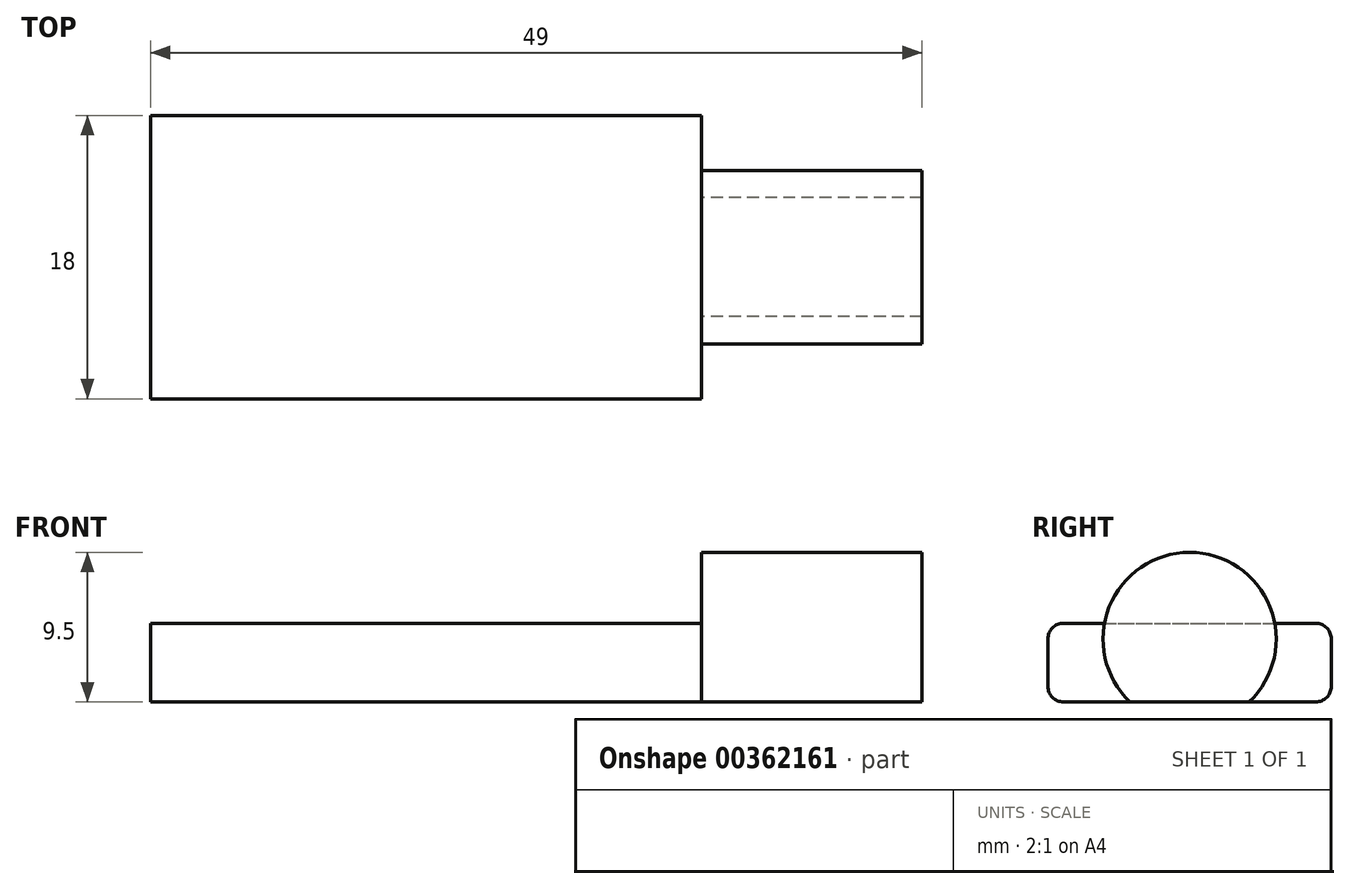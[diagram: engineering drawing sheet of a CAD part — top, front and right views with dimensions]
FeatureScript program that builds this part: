
annotation { "Feature Type Name" : "Feature", "Feature Type Description" : "" }
export const myFeature = defineFeature(function(context is Context, id is Id, definition is map)
    precondition{}
    {
        {
            var Q0;
            Q0=qCreatedBy(makeId("Top.planeOp"),FACE);
            var sketch = newSketch(context, id + "F0", { "sketchPlane" : qUnion([Q0])});
            skLineSegment(sketch, "E0.bottom", {"start": v(0, 0) * mm, "end": v(35, 0) * mm});
            skLineSegment(sketch, "E0.top", {"start": v(0, 18) * mm, "end": v(35, 18) * mm});
            skLineSegment(sketch, "E0.left", {"start": v(0, 0) * mm, "end": v(0, 18) * mm});
            skLineSegment(sketch, "E0.right", {"start": v(35, 0) * mm, "end": v(35, 18) * mm});
            skSolve(sketch);
        }
        {
            var Q0;
            Q0=makeQuery(id+"F0.imprint","IMPRINT",FACE,{"disambiguationData":[TD([[makeQuery(id+"F0.imprint","IMPRINT",EDGE,{"derivedFrom":sQuery(id+"F0.wireOp",EDGE,"E0.bottom")}),1.0]])]});
            extrude(context, id + "F1", {"entities" : qUnion([Q0]), "depth" : 5 * mm});
        }
        {
            var Q0;
            Q0=makeQuery(id+"F1.opExtrude","SWEPT_FACE",FACE,{"disambiguationData":[OSD([sQuery(id+"F0.wireOp",EDGE,"E0.right")])]});
            var sketch = newSketch(context, id + "F2", { "sketchPlane" : qUnion([Q0])});
            skLineSegment(sketch, "E1", {"start": v(0, 4) * mm, "end": v(18, 4) * mm, "construction": true});
            skCircle(sketch, "E2", {"center": v(9, 4) * mm, "radius": 5.5 * mm});
            skLineSegment(sketch, "E3.0", {"start": v(0, 5) * mm, "end": v(0, 0) * mm});
            skSolve(sketch);
        }
        {
            var Q0;
            {var subQ0=sQuery(id+"F2.wireOp",EDGE,"E2");var subQ1=makeQuery(id+"F1.opExtrude","CAP_EDGE",EDGE,{"disambiguationData":[OSD([sQuery(id+"F0.wireOp",EDGE,"E0.right")])],"isStart":false});var subQ2=makeQuery(id+"F2.imprint","INTERSECT",VERTEX,{"disambiguationData":[OD(0.0)],"derivedFrom":[subQ1,subQ0]});Q0=makeQuery(id+"F2.imprint","IMPRINT",FACE,{"disambiguationData":[TD([[makeQuery(id+"F2.imprint","IMPRINT",EDGE,{"disambiguationData":[TD([[subQ2,1.0]])],"derivedFrom":subQ0}),1.0]])]});}
            var Q1;
            {var subQ0=sQuery(id+"F2.wireOp",EDGE,"E2");var subQ1=sQuery(id+"F0.wireOp",EDGE,"E0.right");var subQ2=makeQuery(id+"F1.opExtrude","CAP_EDGE",EDGE,{"disambiguationData":[OSD([subQ1])],"isStart":false});var subQ3=makeQuery(id+"F2.imprint","INTERSECT",VERTEX,{"disambiguationData":[OD(0.0)],"derivedFrom":[subQ2,subQ0]});Q1=makeQuery(id+"F2.imprint","IMPRINT",FACE,{"disambiguationData":[TD([[makeQuery(id+"F2.imprint","IMPRINT",EDGE,{"disambiguationData":[TD([[subQ3,-1.0]])],"derivedFrom":subQ0}),1.0]])]});}
            var Q2;
            {var subQ0=sQuery(id+"F2.wireOp",EDGE,"E2");var subQ1=makeQuery(id+"F1.opExtrude","CAP_EDGE",EDGE,{"disambiguationData":[OSD([sQuery(id+"F0.wireOp",EDGE,"E0.right")])],"isStart":true});var subQ2=makeQuery(id+"F2.imprint","INTERSECT",VERTEX,{"disambiguationData":[OD(0.0)],"derivedFrom":[subQ1,subQ0]});Q2=makeQuery(id+"F2.imprint","IMPRINT",FACE,{"disambiguationData":[TD([[makeQuery(id+"F2.imprint","IMPRINT",EDGE,{"disambiguationData":[TD([[subQ2,-1.0]])],"derivedFrom":subQ0}),1.0]])]});}
            var Q3;
            Q3=sQuery(id+"F2.wireOp",EDGE,"E2");
            extrude(context, id + "F3", {"entities" : qUnion([Q0, Q1, Q2]), "surfaceEntities" : qUnion([Q3]), "depth" : 14 * mm});
        }
        {
            var Q0;
            Q0=makeQuery(id+"F1.opExtrude","CAP_EDGE",EDGE,{"disambiguationData":[OSD([sQuery(id+"F0.wireOp",EDGE,"E0.bottom")])],"isStart":false});
            var Q1;
            Q1=makeQuery(id+"F1.opExtrude","CAP_EDGE",EDGE,{"disambiguationData":[OSD([sQuery(id+"F0.wireOp",EDGE,"E0.top")])],"isStart":false});
            var Q2;
            Q2=makeQuery(id+"F1.opExtrude","CAP_EDGE",EDGE,{"disambiguationData":[OSD([sQuery(id+"F0.wireOp",EDGE,"E0.bottom")])],"isStart":true});
            var Q3;
            Q3=makeQuery(id+"F1.opExtrude","CAP_EDGE",EDGE,{"disambiguationData":[OSD([sQuery(id+"F0.wireOp",EDGE,"E0.top")])],"isStart":true});
            fillet(context, id + "F4", {"entities" : qUnion([Q0, Q1, Q2, Q3]), "radius" : 1 * mm, "allowEdgeOverflow" : false});
        }
    });
